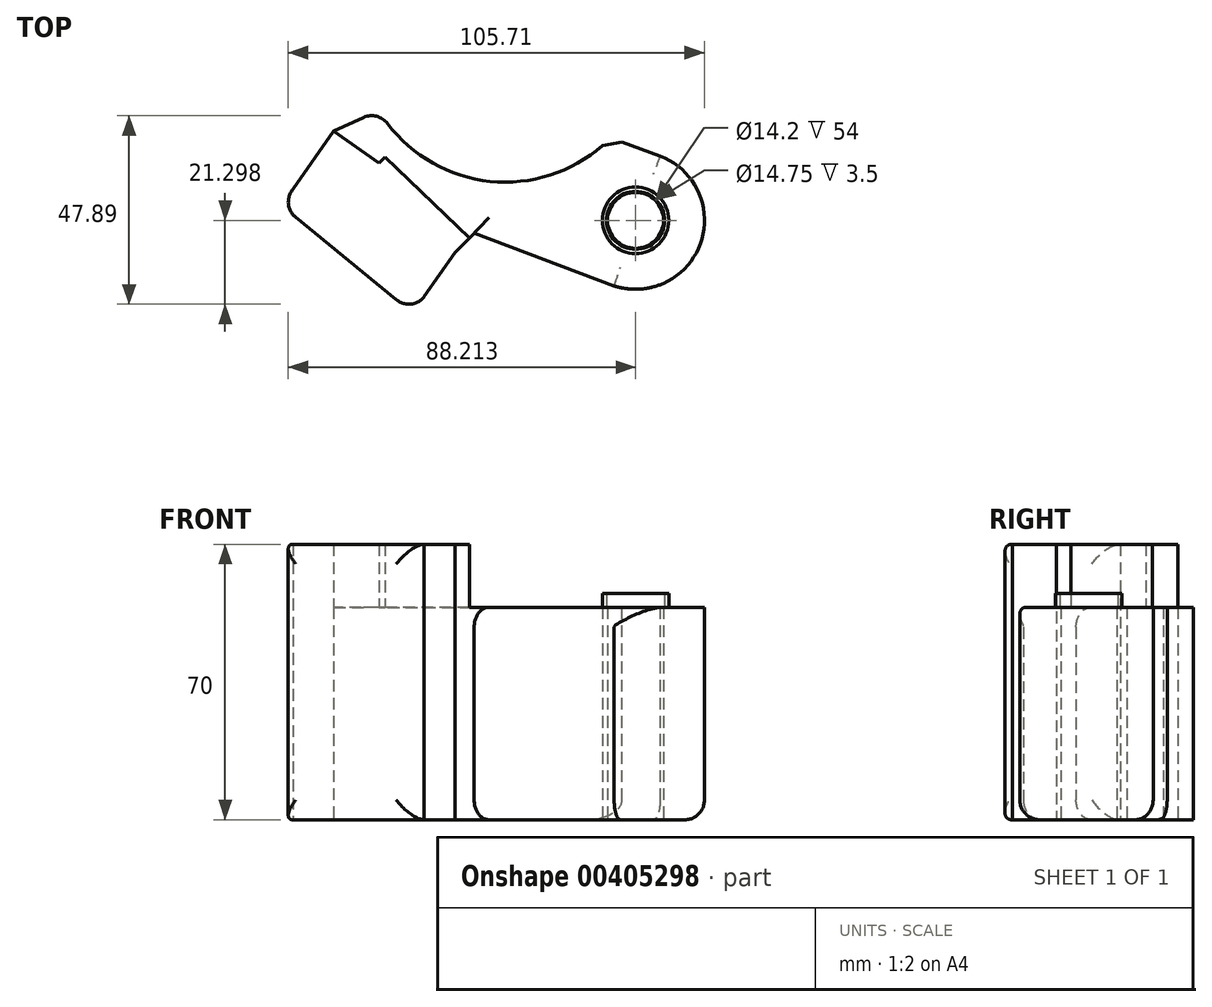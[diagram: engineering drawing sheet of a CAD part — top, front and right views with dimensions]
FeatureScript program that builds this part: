
annotation { "Feature Type Name" : "Feature", "Feature Type Description" : "" }
export const myFeature = defineFeature(function(context is Context, id is Id, definition is map)
    precondition{}
    {
        {
            var Q0;
            Q0=qCreatedBy(makeId("Top.planeOp"),FACE);
            var sketch = newSketch(context, id + "F0", { "sketchPlane" : qUnion([Q0])});
            skPoint(sketch, "E0", {"position": v(0, -20) * mm});
            skPoint(sketch, "E1", {"position": v(-9.5, 0) * mm});
            skPoint(sketch, "E2.10.0", {"position": v(20, 0) * mm});
            skPoint(sketch, "E2.center", {"position": v(0, 0) * mm});
            skLineSegment(sketch, "E3.bottom", {"start": v(20, 0) * mm, "end": v(-20, 0) * mm});
            skLineSegment(sketch, "E3.top", {"start": v(20, -20.23) * mm, "end": v(-20, -20.23) * mm});
            skLineSegment(sketch, "E4.top", {"start": v(9.5, 0) * mm, "end": v(-9.5, 0) * mm});
            skLineSegment(sketch, "E5.left", {"start": v(9.5, 0) * mm, "end": v(9.5, 0) * mm});
            skLineSegment(sketch, "E5.right", {"start": v(-9.5, 0) * mm, "end": v(-9.5, 0) * mm});
            skPoint(sketch, "E6", {"position": v(-22, 0) * mm});
            skLineSegment(sketch, "E7", {"start": v(-22, 0) * mm, "end": v(-20, 0) * mm});
            skLineSegment(sketch, "E8", {"start": v(20, -20.23) * mm, "end": v(33.1, -47.22) * mm});
            skCircle(sketch, "E9", {"center": v(33.1, -47.22) * mm, "radius": 7.1 * mm});
            skCircle(sketch, "E10", {"center": v(33.1, -47.22) * mm, "radius": 17.5 * mm});
            skLineSegment(sketch, "E11", {"start": v(-20, -20.23) * mm, "end": v(20.93, -59.8) * mm});
            skCircle(sketch, "E12", {"center": v(0, 0) * mm, "radius": 35 * mm});
            skCircle(sketch, "E13", {"center": v(0, 0) * mm, "radius": 37.5 * mm});
            skCircle(sketch, "E14", {"center": v(0, 0) * mm, "radius": 50 * mm});
            skLineSegment(sketch, "E15", {"start": v(27.66, -63.86) * mm, "end": v(-17.63, -46.79) * mm});
            skLineSegment(sketch, "E16", {"start": v(39.33, -30.87) * mm, "end": v(26.78, -26.25) * mm});
            skLineSegment(sketch, "E17", {"start": v(-43.57, -24.54) * mm, "end": v(-32.14, -19.33) * mm});
            skLineSegment(sketch, "E18", {"start": v(-43.57, -24.54) * mm, "end": v(-8.4, -49.3) * mm});
            skLineSegment(sketch, "E19", {"start": v(-43.57, -24.54) * mm, "end": v(-53.93, -39.26) * mm});
            skLineSegment(sketch, "E20", {"start": v(-8.4, -49.3) * mm, "end": v(-18.75, -64.01) * mm});
            skLineSegment(sketch, "E21", {"start": v(-53.93, -39.26) * mm, "end": v(-18.75, -64.01) * mm});
            skLineSegment(sketch, "E22", {"start": v(-20, -20.23) * mm, "end": v(-37.39, -38.21) * mm});
            skLineSegment(sketch, "E23", {"start": v(-37.39, -38.21) * mm, "end": v(-16.03, -58.86) * mm});
            skLineSegment(sketch, "E24", {"start": v(-16.03, -58.86) * mm, "end": v(1.36, -40.88) * mm});
            skLineSegment(sketch, "E25", {"start": v(-20, -20.23) * mm, "end": v(-30.5, -31.08) * mm});
            skLineSegment(sketch, "E26", {"start": v(-30.5, -31.08) * mm, "end": v(-9.13, -51.73) * mm});
            skLineSegment(sketch, "E27", {"start": v(-18.75, -64.01) * mm, "end": v(-20.58, -66.6) * mm});
            skLineSegment(sketch, "E28", {"start": v(-53.93, -39.26) * mm, "end": v(-20.58, -66.6) * mm});
            skLineSegment(sketch, "E29", {"start": v(-20.58, -66.6) * mm, "end": v(-23.82, -70.56) * mm});
            skLineSegment(sketch, "E30", {"start": v(-23.82, -70.56) * mm, "end": v(-56.94, -43.4) * mm});
            skLineSegment(sketch, "E31", {"start": v(-56.94, -43.4) * mm, "end": v(-53.93, -39.26) * mm});
            skSolve(sketch);
        }
        {
            var Q0;
            Q0=makeQuery(id+"F0.imprint","IMPRINT",FACE,{"disambiguationData":[TD([[makeQuery(id+"F0.imprint","IMPRINT",EDGE,{"derivedFrom":sQuery(id+"F0.wireOp",EDGE,"E9")}),-1.0]])]});
            var Q1;
            {var subQ0=sQuery(id+"F0.wireOp",EDGE,"E14");var subQ1=sQuery(id+"F0.wireOp",EDGE,"E8");var subQ2=makeQuery(id+"F0.imprint","INTERSECT",VERTEX,{"derivedFrom":[subQ1,subQ0]});Q1=makeQuery(id+"F0.imprint","IMPRINT",FACE,{"disambiguationData":[TD([[makeQuery(id+"F0.imprint","IMPRINT",EDGE,{"disambiguationData":[TD([[subQ2,1.0]])],"derivedFrom":subQ1}),-1.0]])]});}
            var Q2;
            {var subQ0=sQuery(id+"F0.wireOp",EDGE,"E14");var subQ1=sQuery(id+"F0.wireOp",EDGE,"E8");var subQ2=makeQuery(id+"F0.imprint","INTERSECT",VERTEX,{"derivedFrom":[subQ1,subQ0]});Q2=makeQuery(id+"F0.imprint","IMPRINT",FACE,{"disambiguationData":[TD([[makeQuery(id+"F0.imprint","IMPRINT",EDGE,{"disambiguationData":[TD([[subQ2,1.0]])],"derivedFrom":subQ1}),1.0]])]});}
            var Q3;
            {var subQ0=sQuery(id+"F0.wireOp",EDGE,"E13");var subQ1=sQuery(id+"F0.wireOp",EDGE,"E8");var subQ2=makeQuery(id+"F0.imprint","INTERSECT",VERTEX,{"derivedFrom":[subQ1,subQ0]});Q3=makeQuery(id+"F0.imprint","IMPRINT",FACE,{"disambiguationData":[TD([[makeQuery(id+"F0.imprint","IMPRINT",EDGE,{"disambiguationData":[TD([[subQ2,-1.0]])],"derivedFrom":subQ1}),1.0]])]});}
            var Q4;
            {var subQ4=sQuery(id+"F0.wireOp",EDGE,"E13");var subQ7=sQuery(id+"F0.wireOp",EDGE,"E8");var subQ10=makeQuery(id+"F0.imprint","INTERSECT",VERTEX,{"derivedFrom":[subQ7,subQ4]});Q4=makeQuery(id+"F0.imprint","IMPRINT",FACE,{"disambiguationData":[TD([[makeQuery(id+"F0.imprint","IMPRINT",EDGE,{"disambiguationData":[TD([[subQ10,-1.0]])],"derivedFrom":subQ7}),-1.0]])]});}
            var Q5;
            {var subQ0=sQuery(id+"F0.wireOp",EDGE,"E11");var subQ1=sQuery(id+"F0.wireOp",EDGE,"E10");var subQ2=makeQuery(id+"F0.imprint","INTERSECT",VERTEX,{"derivedFrom":[subQ1,subQ0]});Q5=makeQuery(id+"F0.imprint","IMPRINT",FACE,{"disambiguationData":[TD([[makeQuery(id+"F0.imprint","IMPRINT",EDGE,{"disambiguationData":[TD([[subQ2,1.0]])],"derivedFrom":subQ1}),-1.0]])]});}
            var Q6;
            {var subQ1=sQuery(id+"F0.wireOp",EDGE,"E11");var subQ6=sQuery(id+"F0.wireOp",EDGE,"E10");var subQ9=makeQuery(id+"F0.imprint","INTERSECT",VERTEX,{"derivedFrom":[subQ6,subQ1]});Q6=makeQuery(id+"F0.imprint","IMPRINT",FACE,{"disambiguationData":[TD([[makeQuery(id+"F0.imprint","IMPRINT",EDGE,{"disambiguationData":[TD([[subQ9,-1.0]])],"derivedFrom":subQ6}),-1.0]])]});}
            var Q7;
            {var subQ0=sQuery(id+"F0.wireOp",EDGE,"E24");var subQ1=sQuery(id+"F0.wireOp",EDGE,"E11");var subQ2=makeQuery(id+"F0.imprint","INTERSECT",VERTEX,{"derivedFrom":[subQ1,subQ0]});Q7=makeQuery(id+"F0.imprint","IMPRINT",FACE,{"disambiguationData":[TD([[makeQuery(id+"F0.imprint","IMPRINT",EDGE,{"disambiguationData":[TD([[subQ2,-1.0]])],"derivedFrom":subQ1}),-1.0]])]});}
            var Q8;
            {var subQ6=sQuery(id+"F0.wireOp",EDGE,"E11");var subQ10=sQuery(id+"F0.wireOp",EDGE,"E24");var subQ12=makeQuery(id+"F0.imprint","INTERSECT",VERTEX,{"derivedFrom":[subQ6,subQ10]});Q8=makeQuery(id+"F0.imprint","IMPRINT",FACE,{"disambiguationData":[TD([[makeQuery(id+"F0.imprint","IMPRINT",EDGE,{"disambiguationData":[TD([[subQ12,1.0]])],"derivedFrom":subQ6}),-1.0]])]});}
            var Q9;
            {var subQ1=sQuery(id+"F0.wireOp",EDGE,"E17");Q9=makeQuery(id+"F0.imprint","IMPRINT",FACE,{"disambiguationData":[TD([[makeQuery(id+"F0.imprint","IMPRINT",EDGE,{"derivedFrom":subQ1}),-1.0]])]});}
            var Q10;
            {var subQ1=sQuery(id+"F0.wireOp",EDGE,"E14");var subQ3=sQuery(id+"F0.wireOp",EDGE,"E22");var subQ4=makeQuery(id+"F0.imprint","INTERSECT",VERTEX,{"derivedFrom":[subQ1,subQ3]});Q10=makeQuery(id+"F0.imprint","IMPRINT",FACE,{"disambiguationData":[TD([[makeQuery(id+"F0.imprint","IMPRINT",EDGE,{"disambiguationData":[TD([[subQ4,1.0]])],"derivedFrom":subQ3}),-1.0]])]});}
            var Q11;
            {var subQ1=sQuery(id+"F0.wireOp",EDGE,"E19");Q11=makeQuery(id+"F0.imprint","IMPRINT",FACE,{"disambiguationData":[TD([[makeQuery(id+"F0.imprint","IMPRINT",EDGE,{"derivedFrom":subQ1}),1.0]])]});}
            var Q12;
            {var subQ0=sQuery(id+"F0.wireOp",EDGE,"E23");Q12=makeQuery(id+"F0.imprint","IMPRINT",FACE,{"disambiguationData":[TD([[makeQuery(id+"F0.imprint","IMPRINT",EDGE,{"derivedFrom":subQ0}),1.0]])]});}
            var Q13;
            {var subQ1=sQuery(id+"F0.wireOp",EDGE,"E14");var subQ7=makeQuery(id+"F0.imprint","INTERSECT",VERTEX,{"derivedFrom":[subQ1,sQuery(id+"F0.wireOp",EDGE,"E15")]});Q13=makeQuery(id+"F0.imprint","IMPRINT",FACE,{"disambiguationData":[TD([[makeQuery(id+"F0.imprint","IMPRINT",EDGE,{"disambiguationData":[TD([[subQ7,1.0]])],"derivedFrom":subQ1}),1.0]])]});}
            var Q14;
            {var subQ0=sQuery(id+"F0.wireOp",EDGE,"E22");var subQ1=sQuery(id+"F0.wireOp",EDGE,"E18");var subQ2=makeQuery(id+"F0.imprint","INTERSECT",VERTEX,{"derivedFrom":[subQ1,subQ0]});Q14=makeQuery(id+"F0.imprint","IMPRINT",FACE,{"disambiguationData":[TD([[makeQuery(id+"F0.imprint","IMPRINT",EDGE,{"disambiguationData":[TD([[subQ2,-1.0]])],"derivedFrom":subQ1}),1.0]])]});}
            var Q15;
            {var subQ1=sQuery(id+"F0.wireOp",EDGE,"E14");var subQ3=sQuery(id+"F0.wireOp",EDGE,"E26");var subQ4=makeQuery(id+"F0.imprint","INTERSECT",VERTEX,{"derivedFrom":[subQ1,subQ3]});Q15=makeQuery(id+"F0.imprint","IMPRINT",FACE,{"disambiguationData":[TD([[makeQuery(id+"F0.imprint","IMPRINT",EDGE,{"disambiguationData":[TD([[subQ4,1.0]])],"derivedFrom":subQ3}),1.0]])]});}
            var Q16;
            {var subQ0=sQuery(id+"F0.wireOp",EDGE,"E20");var subQ5=sQuery(id+"F0.wireOp",EDGE,"E15");var subQ6=makeQuery(id+"F0.imprint","INTERSECT",VERTEX,{"derivedFrom":[subQ5,subQ0]});Q16=makeQuery(id+"F0.imprint","IMPRINT",FACE,{"disambiguationData":[TD([[makeQuery(id+"F0.imprint","IMPRINT",EDGE,{"disambiguationData":[TD([[subQ6,-1.0]])],"derivedFrom":subQ5}),-1.0]])]});}
            var Q17;
            {var subQ0=sQuery(id+"F0.wireOp",EDGE,"E15");var subQ1=sQuery(id+"F0.wireOp",EDGE,"E14");var subQ2=makeQuery(id+"F0.imprint","INTERSECT",VERTEX,{"derivedFrom":[subQ1,subQ0]});Q17=makeQuery(id+"F0.imprint","IMPRINT",FACE,{"disambiguationData":[TD([[makeQuery(id+"F0.imprint","IMPRINT",EDGE,{"disambiguationData":[TD([[subQ2,-1.0]])],"derivedFrom":subQ1}),-1.0]])]});}
            var Q18;
            {var subQ0=sQuery(id+"F0.wireOp",EDGE,"E20");var subQ1=sQuery(id+"F0.wireOp",EDGE,"E15");var subQ2=makeQuery(id+"F0.imprint","INTERSECT",VERTEX,{"derivedFrom":[subQ1,subQ0]});Q18=makeQuery(id+"F0.imprint","IMPRINT",FACE,{"disambiguationData":[TD([[makeQuery(id+"F0.imprint","IMPRINT",EDGE,{"disambiguationData":[TD([[subQ2,-1.0]])],"derivedFrom":subQ1}),1.0]])]});}
            var Q19;
            {var subQ3=sQuery(id+"F0.wireOp",EDGE,"E24");var subQ5=sQuery(id+"F0.wireOp",EDGE,"E15");var subQ6=makeQuery(id+"F0.imprint","INTERSECT",VERTEX,{"derivedFrom":[subQ5,subQ3]});Q19=makeQuery(id+"F0.imprint","IMPRINT",FACE,{"disambiguationData":[TD([[makeQuery(id+"F0.imprint","IMPRINT",EDGE,{"disambiguationData":[TD([[subQ6,-1.0]])],"derivedFrom":subQ5}),-1.0]])]});}
            var Q20;
            {var subQ0=sQuery(id+"F0.wireOp",EDGE,"E24");var subQ1=sQuery(id+"F0.wireOp",EDGE,"E15");var subQ2=makeQuery(id+"F0.imprint","INTERSECT",VERTEX,{"derivedFrom":[subQ1,subQ0]});Q20=makeQuery(id+"F0.imprint","IMPRINT",FACE,{"disambiguationData":[TD([[makeQuery(id+"F0.imprint","IMPRINT",EDGE,{"disambiguationData":[TD([[subQ2,-1.0]])],"derivedFrom":subQ1}),1.0]])]});}
            var Q21;
            {var subQ0=sQuery(id+"F0.wireOp",EDGE,"E24");var subQ1=sQuery(id+"F0.wireOp",EDGE,"E20");var subQ2=makeQuery(id+"F0.imprint","INTERSECT",VERTEX,{"derivedFrom":[subQ1,subQ0]});Q21=makeQuery(id+"F0.imprint","IMPRINT",FACE,{"disambiguationData":[TD([[makeQuery(id+"F0.imprint","IMPRINT",EDGE,{"disambiguationData":[TD([[subQ2,1.0]])],"derivedFrom":subQ1}),1.0]])]});}
            extrude(context, id + "F1", {"entities" : qUnion([Q0, Q1, Q2, Q3, Q4, Q5, Q6, Q7, Q8, Q9, Q10, Q11, Q12, Q13, Q14, Q15, Q16, Q17, Q18, Q19, Q20, Q21]), "depth" : 54 * mm});
        }
        {
            var Q0;
            {var subQ1=sQuery(id+"F0.wireOp",EDGE,"E19");Q0=makeQuery(id+"F0.imprint","IMPRINT",FACE,{"disambiguationData":[TD([[makeQuery(id+"F0.imprint","IMPRINT",EDGE,{"derivedFrom":subQ1}),1.0]])]});}
            var Q1;
            {var subQ0=sQuery(id+"F0.wireOp",EDGE,"E23");Q1=makeQuery(id+"F0.imprint","IMPRINT",FACE,{"disambiguationData":[TD([[makeQuery(id+"F0.imprint","IMPRINT",EDGE,{"derivedFrom":subQ0}),1.0]])]});}
            var Q2;
            {var subQ1=sQuery(id+"F0.wireOp",EDGE,"E14");var subQ7=makeQuery(id+"F0.imprint","INTERSECT",VERTEX,{"derivedFrom":[subQ1,sQuery(id+"F0.wireOp",EDGE,"E15")]});Q2=makeQuery(id+"F0.imprint","IMPRINT",FACE,{"disambiguationData":[TD([[makeQuery(id+"F0.imprint","IMPRINT",EDGE,{"disambiguationData":[TD([[subQ7,1.0]])],"derivedFrom":subQ1}),1.0]])]});}
            var Q3;
            {var subQ0=sQuery(id+"F0.wireOp",EDGE,"E22");var subQ1=sQuery(id+"F0.wireOp",EDGE,"E18");var subQ2=makeQuery(id+"F0.imprint","INTERSECT",VERTEX,{"derivedFrom":[subQ1,subQ0]});Q3=makeQuery(id+"F0.imprint","IMPRINT",FACE,{"disambiguationData":[TD([[makeQuery(id+"F0.imprint","IMPRINT",EDGE,{"disambiguationData":[TD([[subQ2,-1.0]])],"derivedFrom":subQ1}),1.0]])]});}
            var Q4;
            {var subQ1=sQuery(id+"F0.wireOp",EDGE,"E14");var subQ3=sQuery(id+"F0.wireOp",EDGE,"E22");var subQ4=makeQuery(id+"F0.imprint","INTERSECT",VERTEX,{"derivedFrom":[subQ1,subQ3]});Q4=makeQuery(id+"F0.imprint","IMPRINT",FACE,{"disambiguationData":[TD([[makeQuery(id+"F0.imprint","IMPRINT",EDGE,{"disambiguationData":[TD([[subQ4,1.0]])],"derivedFrom":subQ3}),-1.0]])]});}
            var Q5;
            {var subQ0=sQuery(id+"F0.wireOp",EDGE,"E15");var subQ1=sQuery(id+"F0.wireOp",EDGE,"E14");var subQ2=makeQuery(id+"F0.imprint","INTERSECT",VERTEX,{"derivedFrom":[subQ1,subQ0]});Q5=makeQuery(id+"F0.imprint","IMPRINT",FACE,{"disambiguationData":[TD([[makeQuery(id+"F0.imprint","IMPRINT",EDGE,{"disambiguationData":[TD([[subQ2,-1.0]])],"derivedFrom":subQ1}),-1.0]])]});}
            var Q6;
            {var subQ0=sQuery(id+"F0.wireOp",EDGE,"E24");var subQ1=sQuery(id+"F0.wireOp",EDGE,"E20");var subQ2=makeQuery(id+"F0.imprint","INTERSECT",VERTEX,{"derivedFrom":[subQ1,subQ0]});Q6=makeQuery(id+"F0.imprint","IMPRINT",FACE,{"disambiguationData":[TD([[makeQuery(id+"F0.imprint","IMPRINT",EDGE,{"disambiguationData":[TD([[subQ2,1.0]])],"derivedFrom":subQ1}),1.0]])]});}
            var Q7;
            Q7=makeQuery(id+"F0.imprint","IMPRINT",FACE,{"disambiguationData":[TD([[makeQuery(id+"F0.imprint","IMPRINT",EDGE,{"derivedFrom":sQuery(id+"F0.wireOp",EDGE,"E21")}),-1.0]])]});
            var Q8;
            Q8=makeQuery(id+"F0.imprint","IMPRINT",FACE,{"disambiguationData":[TD([[makeQuery(id+"F0.imprint","IMPRINT",EDGE,{"derivedFrom":sQuery(id+"F0.wireOp",EDGE,"E28")}),-1.0]])]});
            extrude(context, id + "F2", {"entities" : qUnion([Q0, Q1, Q2, Q3, Q4, Q5, Q6, Q7, Q8]), "operationType" : NewBodyOperationType.ADD, "depth" : 70 * mm});
        }
        {
            var Q0;
            Q0=makeQuery(id+"F1.opExtrude","SWEPT_EDGE",EDGE,{"disambiguationData":[OSD([sQuery(id+"F0.wireOp",EDGE,"E13"),sQuery(id+"F0.wireOp",EDGE,"E16")])]});
            chamfer(context, id + "F3", {"entities" : qUnion([Q0]), "width" : 5 * mm, "tangentPropagation" : true});
        }
        {
            var Q0;
            Q0=makeQuery(id+"F1.opExtrude","CAP_FACE",FACE,{"disambiguationData":[OSD([sQuery(id+"F0.wireOp",EDGE,"E9"),sQuery(id+"F0.wireOp",EDGE,"E10"),sQuery(id+"F0.wireOp",EDGE,"E13"),sQuery(id+"F0.wireOp",EDGE,"E15"),sQuery(id+"F0.wireOp",EDGE,"E16"),sQuery(id+"F0.wireOp",EDGE,"E17"),sQuery(id+"F0.wireOp",EDGE,"E19"),sQuery(id+"F0.wireOp",EDGE,"E20"),sQuery(id+"F0.wireOp",EDGE,"E21"),sQuery(id+"F0.wireOp",EDGE,"E24")])],"isStart":false});
            var sketch = newSketch(context, id + "F4", { "sketchPlane" : qUnion([Q0])});
            skCircle(sketch, "E32", {"center": v(33.1, -47.22) * mm, "radius": 8.44 * mm});
            skCircle(sketch, "E33", {"center": v(33.1, -47.22) * mm, "radius": 7.38 * mm});
            skSolve(sketch);
        }
        {
            var Q0;
            Q0=makeQuery(id+"F4.imprint","IMPRINT",FACE,{"disambiguationData":[TD([[makeQuery(id+"F4.imprint","IMPRINT",EDGE,{"derivedFrom":sQuery(id+"F4.wireOp",EDGE,"E32")}),1.0]])]});
            extrude(context, id + "F5", {"entities" : qUnion([Q0]), "operationType" : NewBodyOperationType.ADD, "depth" : 3.5 * mm});
        }
        {
            var Q0;
            Q0=makeQuery(id+"F1.opExtrude","CAP_EDGE",EDGE,{"disambiguationData":[OSD([sQuery(id+"F0.wireOp",EDGE,"E15")])],"isStart":false});
            var Q1;
            Q1=makeQuery(id+"F1.opExtrude","CAP_EDGE",EDGE,{"disambiguationData":[OSD([sQuery(id+"F0.wireOp",EDGE,"E15")])],"isStart":true});
            var Q2;
            Q2=makeQuery(id+"F1.opExtrude","CAP_EDGE",EDGE,{"disambiguationData":[OSD([sQuery(id+"F0.wireOp",EDGE,"E10")])],"isStart":true});
            var Q3;
            Q3=makeQuery(id+"F1.opExtrude","CAP_EDGE",EDGE,{"disambiguationData":[OSD([sQuery(id+"F0.wireOp",EDGE,"E16")])],"isStart":true});
            var Q4;
            Q4=makeQuery(id+"F1.opExtrude","SWEPT_EDGE",EDGE,{"disambiguationData":[OSD([sQuery(id+"F0.wireOp",EDGE,"E13"),sQuery(id+"F0.wireOp",EDGE,"E17")])]});
            fillet(context, id + "F6", {"entities" : qUnion([Q0, Q1, Q2, Q3, Q4]), "radius" : 5 * mm, "tangentPropagation" : true, "allowEdgeOverflow" : false});
        }
        {
            var Q0;
            Q0=makeQuery(id+"F2.opExtrude","SWEPT_EDGE",EDGE,{"disambiguationData":[OSD([sQuery(id+"F0.wireOp",EDGE,"E29"),sQuery(id+"F0.wireOp",EDGE,"E30")])]});
            var Q1;
            Q1=makeQuery(id+"F2.opExtrude","SWEPT_EDGE",EDGE,{"disambiguationData":[OSD([sQuery(id+"F0.wireOp",EDGE,"E30"),sQuery(id+"F0.wireOp",EDGE,"E31")])]});
            var Q2;
            Q2=makeQuery(id+"F2.opExtrude","CAP_EDGE",EDGE,{"disambiguationData":[OSD([sQuery(id+"F0.wireOp",EDGE,"E30")])],"isStart":true});
            var Q3;
            Q3=makeQuery(id+"F2.opExtrude","CAP_EDGE",EDGE,{"disambiguationData":[OSD([sQuery(id+"F0.wireOp",EDGE,"E30")])],"isStart":false});
            fillet(context, id + "F7", {"entities" : qUnion([Q0, Q1, Q2, Q3]), "radius" : 5 * mm, "tangentPropagation" : true, "allowEdgeOverflow" : false});
        }
    });
